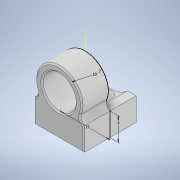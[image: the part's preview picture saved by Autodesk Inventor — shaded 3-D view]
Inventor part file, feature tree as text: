
AUTODESK INVENTOR PART (.ipt)
format: ipt  version: 2021 (Build 250183000, 183)  size: 419,328 bytes
history: native  units: mm
features: extrude x3, sketch x2, chamfer x2, fillet x2, other x1
ambient origin geometry x8: Origin, YZ Plane, XZ Plane, XY Plane, X Axis, Y Axis, Z Axis, Center Point
bodies: Solid1 (feature_tree)
feature tree (10):
  sketch  "Sketch1"  dims[d0=10.0mm d1=2.0mm]
  extrude  "Extrusion1"  Depth=10.0mm
  extrude  "Extrusion2"  Depth=10.0mm
  other  "Work Point1"
  extrude  "Extrusion3"  Depth=8.0mm TaperAngle=0.0deg
  chamfer  "Chamfer1"  Distance=8.0mm
  fillet  "Fillet1"  Radius=3.2mm
  fillet  "Fillet2"  Radius=10.0mm
  chamfer  "Chamfer2"  Distance=2.0mm Angle=45.0deg
  sketch  "Sketch2"  dims[d2=7.0mm d3=15.0mm d4=8.0mm d5=0.0mm d6=8.0mm d7=0.0mm d8=3.2mm d9=10.0mm d10=0.0mm d11=2.0mm d12=2.0mm d13=45.0deg d14=2.0mm d15=0.4mm d16=0.4mm d17=2.0mm d18=45.0deg]
